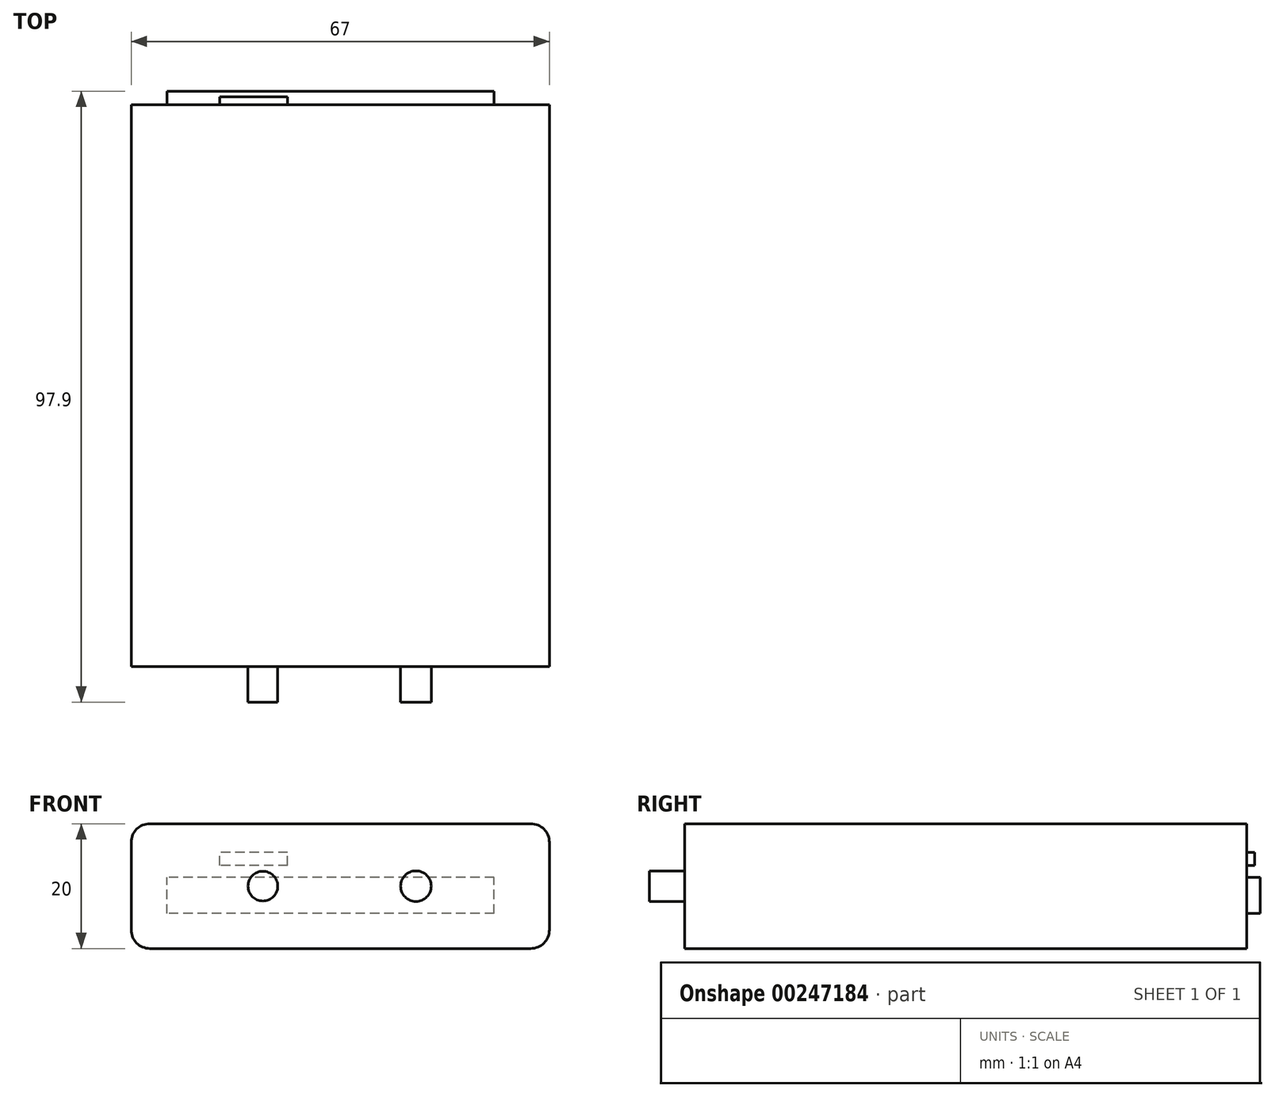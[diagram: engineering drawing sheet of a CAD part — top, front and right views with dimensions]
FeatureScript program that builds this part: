
annotation { "Feature Type Name" : "Feature", "Feature Type Description" : "" }
export const myFeature = defineFeature(function(context is Context, id is Id, definition is map)
    precondition{}
    {
        {
            var Q0;
            Q0=qCreatedBy(makeId("Front.planeOp"),FACE);
            var sketch = newSketch(context, id + "F0", { "sketchPlane" : qUnion([Q0])});
            skLineSegment(sketch, "E0.bottom", {"start": v(33.5, -10) * mm, "end": v(-33.5, -10) * mm});
            skLineSegment(sketch, "E0.top", {"start": v(33.5, 10) * mm, "end": v(-33.5, 10) * mm});
            skLineSegment(sketch, "E0.left", {"start": v(33.5, -10) * mm, "end": v(33.5, 10) * mm});
            skLineSegment(sketch, "E0.right", {"start": v(-33.5, -10) * mm, "end": v(-33.5, 10) * mm});
            skPoint(sketch, "E0.middle", {"position": v(0, 0) * mm});
            skSolve(sketch);
        }
        {
            var Q0;
            Q0=makeQuery(id+"F0.imprint","IMPRINT",FACE,{"disambiguationData":[TD([[makeQuery(id+"F0.imprint","IMPRINT",EDGE,{"derivedFrom":sQuery(id+"F0.wireOp",EDGE,"E0.bottom")}),-1.0]])]});
            extrude(context, id + "F1", {"entities" : qUnion([Q0]), "endBound" : BoundingType.SYMMETRIC, "depth" : 90 * mm});
        }
        {
            var Q0;
            Q0=makeQuery(id+"F1.opExtrude","SWEPT_EDGE",EDGE,{"disambiguationData":[OSD([sQuery(id+"F0.wireOp",EDGE,"E0.top"),sQuery(id+"F0.wireOp",EDGE,"E0.right")])]});
            var Q1;
            Q1=makeQuery(id+"F1.opExtrude","SWEPT_EDGE",EDGE,{"disambiguationData":[OSD([sQuery(id+"F0.wireOp",EDGE,"E0.bottom"),sQuery(id+"F0.wireOp",EDGE,"E0.right")])]});
            var Q2;
            Q2=makeQuery(id+"F1.opExtrude","SWEPT_EDGE",EDGE,{"disambiguationData":[OSD([sQuery(id+"F0.wireOp",EDGE,"E0.top"),sQuery(id+"F0.wireOp",EDGE,"E0.left")])]});
            var Q3;
            Q3=makeQuery(id+"F1.opExtrude","SWEPT_EDGE",EDGE,{"disambiguationData":[OSD([sQuery(id+"F0.wireOp",EDGE,"E0.bottom"),sQuery(id+"F0.wireOp",EDGE,"E0.left")])]});
            fillet(context, id + "F2", {"entities" : qUnion([Q0, Q1, Q2, Q3]), "radius" : 3 * mm, "tangentPropagation" : true, "allowEdgeOverflow" : false});
        }
        {
            var Q0;
            Q0=makeQuery(id+"F1.opExtrude","CAP_FACE",FACE,{"disambiguationData":[OSD([sQuery(id+"F0.wireOp",EDGE,"E0.bottom"),sQuery(id+"F0.wireOp",EDGE,"E0.top"),sQuery(id+"F0.wireOp",EDGE,"E0.left"),sQuery(id+"F0.wireOp",EDGE,"E0.right")])],"isStart":false});
            var sketch = newSketch(context, id + "F3", { "sketchPlane" : qUnion([Q0])});
            skLineSegment(sketch, "E1", {"start": v(-33.5, 0) * mm, "end": v(33.5, 0) * mm});
            skCircle(sketch, "E2", {"center": v(-12.4, 0) * mm, "radius": 2.38 * mm});
            skCircle(sketch, "E3", {"center": v(12.12, 0) * mm, "radius": 2.45 * mm});
            skSolve(sketch);
        }
        {
            var Q0;
            Q0 = qSketchRegion(id + "F3", true);
            extrude(context, id + "F4", {"entities" : qUnion([Q0]), "operationType" : NewBodyOperationType.ADD, "depth" : 5.6 * mm});
        }
        {
            var Q0;
            Q0 = qSketchRegion(id + "F3", true);
            extrude(context, id + "F5", {"entities" : qUnion([Q0]), "operationType" : NewBodyOperationType.ADD, "depth" : 5.7 * mm});
        }
        {
            var Q0;
            Q0=makeQuery(id+"F1.opExtrude","CAP_FACE",FACE,{"disambiguationData":[OSD([sQuery(id+"F0.wireOp",EDGE,"E0.bottom"),sQuery(id+"F0.wireOp",EDGE,"E0.top"),sQuery(id+"F0.wireOp",EDGE,"E0.left"),sQuery(id+"F0.wireOp",EDGE,"E0.right")])],"isStart":true});
            var sketch = newSketch(context, id + "F6", { "sketchPlane" : qUnion([Q0])});
            skLineSegment(sketch, "E4.bottom", {"start": v(-24.65, -4.39) * mm, "end": v(27.74, -4.39) * mm});
            skLineSegment(sketch, "E4.top", {"start": v(-24.65, 1.42) * mm, "end": v(27.74, 1.42) * mm});
            skLineSegment(sketch, "E4.left", {"start": v(-24.65, -4.39) * mm, "end": v(-24.65, 1.42) * mm});
            skLineSegment(sketch, "E4.right", {"start": v(27.74, -4.39) * mm, "end": v(27.74, 1.42) * mm});
            skLineSegment(sketch, "E5.bottom", {"start": v(8.43, 3.31) * mm, "end": v(19.29, 3.31) * mm});
            skLineSegment(sketch, "E5.top", {"start": v(8.43, 5.43) * mm, "end": v(19.29, 5.43) * mm});
            skLineSegment(sketch, "E5.left", {"start": v(8.43, 3.31) * mm, "end": v(8.43, 5.43) * mm});
            skLineSegment(sketch, "E5.right", {"start": v(19.29, 3.31) * mm, "end": v(19.29, 5.43) * mm});
            skSolve(sketch);
        }
        {
            var Q0;
            Q0=makeQuery(id+"F6.imprint","IMPRINT",FACE,{"disambiguationData":[TD([[makeQuery(id+"F6.imprint","IMPRINT",EDGE,{"derivedFrom":sQuery(id+"F6.wireOp",EDGE,"E4.bottom")}),1.0]])]});
            extrude(context, id + "F7", {"entities" : qUnion([Q0]), "operationType" : NewBodyOperationType.ADD, "depth" : 2.2 * mm});
        }
        {
            var Q0;
            Q0=makeQuery(id+"F6.imprint","IMPRINT",FACE,{"disambiguationData":[TD([[makeQuery(id+"F6.imprint","IMPRINT",EDGE,{"derivedFrom":sQuery(id+"F6.wireOp",EDGE,"E5.bottom")}),1.0]])]});
            extrude(context, id + "F8", {"entities" : qUnion([Q0]), "operationType" : NewBodyOperationType.ADD, "depth" : 1.3 * mm});
        }
    });
